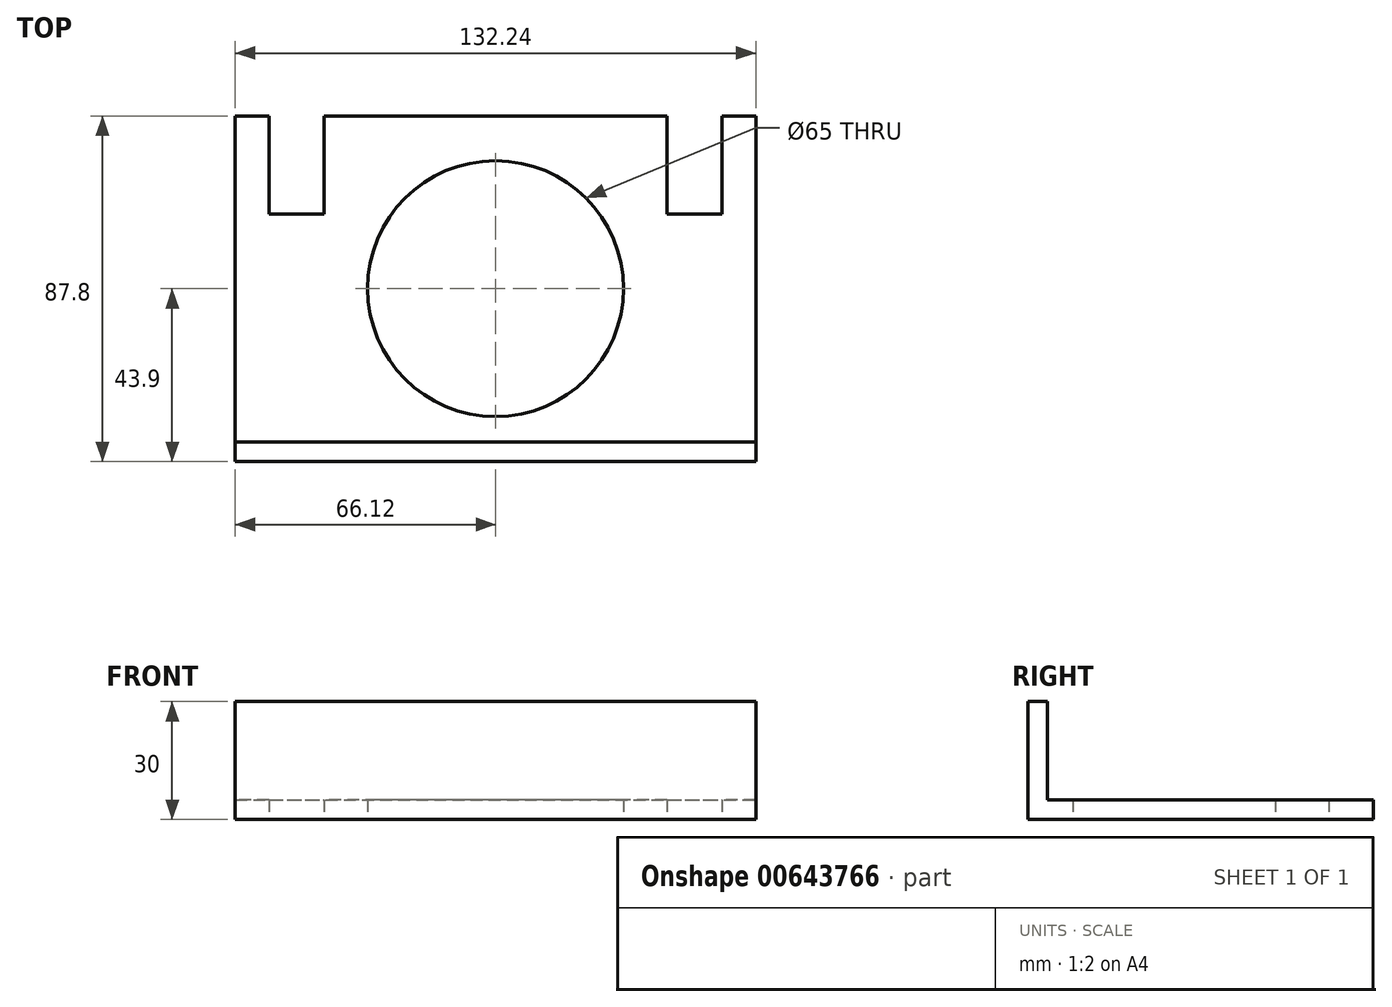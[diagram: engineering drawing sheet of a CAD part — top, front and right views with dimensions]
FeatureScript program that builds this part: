
annotation { "Feature Type Name" : "Feature", "Feature Type Description" : "" }
export const myFeature = defineFeature(function(context is Context, id is Id, definition is map)
    precondition{}
    {
        {
            var Q0;
            Q0=qCreatedBy(makeId("Top.planeOp"),FACE);
            var sketch = newSketch(context, id + "F0", { "sketchPlane" : qUnion([Q0])});
            skLineSegment(sketch, "E0.bottom", {"start": v(66.12, 43.9) * mm, "end": v(-66.12, 43.9) * mm});
            skLineSegment(sketch, "E0.top", {"start": v(66.12, -43.9) * mm, "end": v(-66.12, -43.9) * mm});
            skLineSegment(sketch, "E0.left", {"start": v(66.12, 43.9) * mm, "end": v(66.12, -43.9) * mm});
            skLineSegment(sketch, "E0.right", {"start": v(-66.12, 43.9) * mm, "end": v(-66.12, -43.9) * mm});
            skPoint(sketch, "E0.middle", {"position": v(0, 0) * mm});
            skCircle(sketch, "E1", {"center": v(0, 0) * mm, "radius": 32.5 * mm});
            skLineSegment(sketch, "E2.bottom", {"start": v(-57.55, 43.9) * mm, "end": v(-43.55, 43.9) * mm});
            skLineSegment(sketch, "E2.top", {"start": v(-57.55, 18.9) * mm, "end": v(-43.55, 18.9) * mm});
            skLineSegment(sketch, "E2.left", {"start": v(-57.55, 43.9) * mm, "end": v(-57.55, 18.9) * mm});
            skLineSegment(sketch, "E2.right", {"start": v(-43.55, 43.9) * mm, "end": v(-43.55, 18.9) * mm});
            skLineSegment(sketch, "E3.bottom", {"start": v(43.55, 43.9) * mm, "end": v(57.55, 43.9) * mm});
            skLineSegment(sketch, "E3.top", {"start": v(43.55, 18.9) * mm, "end": v(57.55, 18.9) * mm});
            skLineSegment(sketch, "E3.left", {"start": v(43.55, 43.9) * mm, "end": v(43.55, 18.9) * mm});
            skLineSegment(sketch, "E3.right", {"start": v(57.55, 43.9) * mm, "end": v(57.55, 18.9) * mm});
            skSolve(sketch);
        }
        {
            var Q0;
            Q0=makeQuery(id+"F0.imprint","IMPRINT",FACE,{"disambiguationData":[TD([[makeQuery(id+"F0.imprint","IMPRINT",EDGE,{"derivedFrom":sQuery(id+"F0.wireOp",EDGE,"E0.top")}),-1.0]])]});
            extrude(context, id + "F1", {"entities" : qUnion([Q0]), "depth" : 5 * mm, "offsetDistance" : 25 * mm});
        }
        {
            var Q0;
            Q0=makeQuery(id+"F1.opExtrude","CAP_FACE",FACE,{"disambiguationData":[OSD([sQuery(id+"F0.wireOp",EDGE,"E0.bottom"),sQuery(id+"F0.wireOp",EDGE,"E0.top"),sQuery(id+"F0.wireOp",EDGE,"E0.left"),sQuery(id+"F0.wireOp",EDGE,"E0.right"),sQuery(id+"F0.wireOp",EDGE,"E1"),sQuery(id+"F0.wireOp",EDGE,"E2.top"),sQuery(id+"F0.wireOp",EDGE,"E2.left"),sQuery(id+"F0.wireOp",EDGE,"E2.right"),sQuery(id+"F0.wireOp",EDGE,"E3.top"),sQuery(id+"F0.wireOp",EDGE,"E3.left"),sQuery(id+"F0.wireOp",EDGE,"E3.right")])],"isStart":false});
            var sketch = newSketch(context, id + "F2", { "sketchPlane" : qUnion([Q0])});
            skLineSegment(sketch, "E4.bottom", {"start": v(-66.12, -43.9) * mm, "end": v(66.12, -43.9) * mm});
            skLineSegment(sketch, "E4.top", {"start": v(-66.12, -38.9) * mm, "end": v(66.12, -38.9) * mm});
            skLineSegment(sketch, "E4.left", {"start": v(-66.12, -43.9) * mm, "end": v(-66.12, -38.9) * mm});
            skLineSegment(sketch, "E4.right", {"start": v(66.12, -43.9) * mm, "end": v(66.12, -38.9) * mm});
            skSolve(sketch);
        }
        {
            var Q0;
            Q0=makeQuery(id+"F2.imprint","IMPRINT",FACE,{"disambiguationData":[TD([[makeQuery(id+"F2.imprint","IMPRINT",EDGE,{"derivedFrom":sQuery(id+"F2.wireOp",EDGE,"E4.bottom")}),-1.0]])]});
            extrude(context, id + "F3", {"entities" : qUnion([Q0]), "operationType" : NewBodyOperationType.ADD, "depth" : 25 * mm, "offsetDistance" : 25 * mm});
        }
    });
